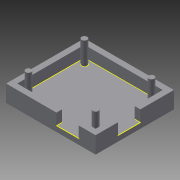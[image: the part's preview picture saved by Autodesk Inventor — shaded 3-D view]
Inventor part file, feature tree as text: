
AUTODESK INVENTOR PART (.ipt)
format: ipt  version: 2014 SP1 (Build 180222100, 222)  size: 142,336 bytes
history: native  units: in
note: dims shown in document units (in); Inventor stores cm internally (conversion verified against a paired STEP export)
features: sketch x6, extrude x5
ambient origin geometry x8: Origin, YZ Plane, XZ Plane, XY Plane, X Axis, Y Axis, Z Axis, Center Point
bodies: Solid1 (feature_tree)
feature tree (11):
  extrude  "Extrusion1"  Depth=2.0in
  extrude  "Extrusion2"  Depth=0.125in
  extrude  "Extrusion3"  Depth=0.125in
  extrude  "Extrusion4"  Depth=0.25in TaperAngle=0.0deg
  extrude  "Extrusion5"  Depth=0.125in
  sketch  "Sketch6"  dims[d12=0.125in d13=0.125in d14=0.125in d15=0.125in d16=0.125in d17=0.125in d18=0.125in d19=0.125in d20=0.125in d21=0.125in d22=0.5in d23=0.0in d24=0.25in d25=1.125in d27=1.625in d28=0.125in d29=0.0in d30=0.5in d31=1.0in d32=0.25in d33=0.125in d34=0.0in]
  sketch  "Sketch1"  dims[d0=1.75in d1=2.0in]
  sketch  "Sketch2"  dims[d2=0.125in d3=0.0in d4=0.125in]
  sketch  "Sketch3"  dims[d5=0.125in d6=0.125in]
  sketch  "Sketch4"  dims[d7=0.125in d8=0.25in d9=0.0in]
  sketch  "Sketch5"  dims[d10=0.125in d11=0.125in]
